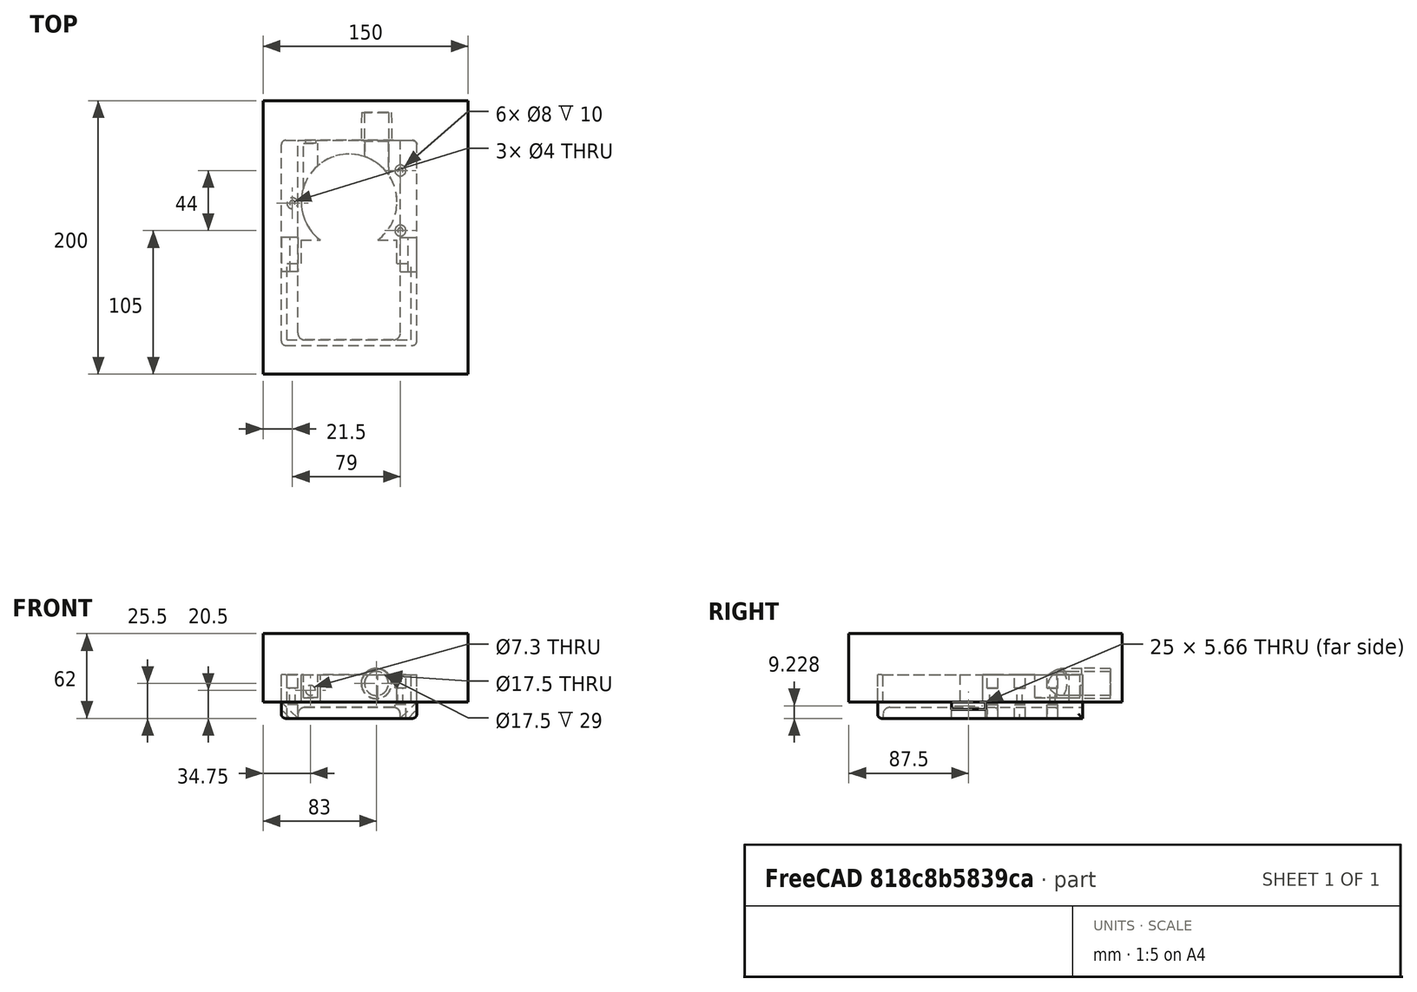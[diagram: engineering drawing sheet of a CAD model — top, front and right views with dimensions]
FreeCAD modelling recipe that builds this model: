
FCSTD DOCUMENT  (FreeCAD 0.18R4 (GitTag))
Label: PAPR-LOWER-V2
License: All rights reserved
LicenseURL: http://en.wikipedia.org/wiki/All_rights_reserved
objects: Part::Cylinder×17, Part::MultiFuse×11, Part::Box×8, Part::Fillet×7, Part::Cut×3, Part::Cone×2, Part::FeaturePython×1, Part::Mirroring×1
note: 50 computed .brp shape members not serialized (recipe doc carries the construction recipe); baked Part::Feature solids carry a one-line shape summary decoded from their .brp

FEATURE [Part::Cylinder] Cylinder  label="BlowerBody"
  Angle = 360
  AttacherType = Attacher::AttachEngine3D
  Height = 18
  Placement = pos=(0,0,4.5) rot=(0,0,1;0rad)
  Radius = 35
FEATURE [Part::Cylinder] Cylinder001  label="BlowerEndbearing"
  Angle = 360
  AttacherType = Attacher::AttachEngine3D
  Height = 5
  Placement = pos=(0,0,1) rot=(0,0,1;0rad)
  Radius = 2.25
FEATURE [Part::Cylinder] Cylinder002
  Angle = 360
  AttacherType = Attacher::AttachEngine3D
  Height = 10
  Placement = pos=(0,-28.4,0) rot=(0,0,1;0rad)
  Radius = 2
FEATURE [Part::FeaturePython] Array  label="BlowerFeet"  # Draft array (typed FeaturePython)
  Angle = 360
  ArrayType = 1
  Axis = (0,0,1)
  Base = -> Cylinder002
  Center = (0,0,0)
  Fuse = false
  IntervalAxis = (0,0,0)
  IntervalX = (1,0,0)
  IntervalY = (0,1,0)
  IntervalZ = (0,0,1)
  NumberPolar = 3
  NumberX = 1
  NumberY = 1
  NumberZ = 1
FEATURE [Part::Cylinder] Cylinder003  label="BlowerOutlet"
  Angle = 360
  AttacherType = Attacher::AttachEngine3D
  Height = 40
  Placement = pos=(20,36.3,13.5) rot=(1,0,0;1.5708rad)
  Radius = 8.75
FEATURE [Part::Cone] Cone  label="BlowerInlet"
  Angle = 360
  AttacherType = Attacher::AttachEngine3D
  Height = 13
  Placement = pos=(0,0,22.5) rot=(0,0,1;0rad)
  Radius1 = 27.25
  Radius2 = 27.15
FEATURE [Part::Cylinder] Cylinder004  label="BlowerBodyEnvelope"
  Angle = 360
  AttacherType = Attacher::AttachEngine3D
  Height = 25
  Radius = 35
FEATURE [Part::Cylinder] Cylinder005  label="OutletExtension"
  Angle = 360
  AttacherType = Attacher::AttachEngine3D
  Height = 40
  Placement = pos=(20,65.3,13.5) rot=(1,0,0;1.5708rad)
  Radius = 8.75
FEATURE [Part::Box] Box  label="DriverPocket"
  AttacherType = Attacher::AttachEngine3D
  Height = 20
  Length = 91
  Placement = pos=(-45.5,-106,0) rot=(0,0,1;0rad)
  Width = 56
FEATURE [Part::Box] Box001  label="WiringPocket"
  AttacherType = Attacher::AttachEngine3D
  Height = 20
  Length = 70
  Placement = pos=(-35,-53,0) rot=(0,0,1;0rad)
  Width = 20
FEATURE [Part::MultiFuse] Fusion  label="ElectronicsPocket"
  Placement = pos=(0,5,0) rot=(0,0,1;0rad)
  Shapes = -> [Box,Box001]
FEATURE [Part::Box] Box002  label="Potentiometer"
  AttacherType = Attacher::AttachEngine3D
  Height = 17
  Length = 10.5
  Placement = pos=(-30,18,5.5) rot=(0,0,1;0rad)
  Width = 35
FEATURE [Part::Cylinder] Cylinder006  label="Cylinder"
  Angle = 360
  AttacherType = Attacher::AttachEngine3D
  Height = 10
  Placement = pos=(-24.75,60.5,11) rot=(1,0,0;1.5708rad)
  Radius = 3.65
FEATURE [Part::MultiFuse] Fusion001  label="PotPocket"
  Placement = pos=(-3.5,-10,-2.5) rot=(0,0,1;0rad)
  Shapes = -> [Cylinder006,Box002]
FEATURE [Part::Box] Box003  label="Cube"
  AttacherType = Attacher::AttachEngine3D
  Height = 25
  Length = 75
  Placement = pos=(-37.5,-101,-29) rot=(0,0,1;0rad)
  Width = 150
FEATURE [Part::Fillet] Fillet
  Base = -> Box003
  Edges = 1 edges r=5: [Edge2]
FEATURE [Part::Fillet] Fillet001
  Base = -> Fillet
  Edges = 1 edges r=5: [Edge3]
FEATURE [Part::Fillet] Fillet002
  Base = -> Fillet001
  Edges = 1 edges r=5: [Edge17]
FEATURE [Part::Fillet] Fillet003
  Base = -> Fillet002
  Edges = 1 edges r=5: [Edge15]
FEATURE [Part::Fillet] Fillet004
  Base = -> Fillet003
  Edges = 1 edges r=5: [Edge18]
FEATURE [Part::Fillet] Fillet005  label="BatteryPocket"
  Base = -> Fillet004
  Edges = 4 edges r=5: [Edge3,Edge12,Edge13,Edge16]
FEATURE [Part::Box] Box004  label="HousingBlock"
  AttacherType = Attacher::AttachEngine3D
  Height = 32
  Length = 99
  Placement = pos=(-49.5,-105,-12) rot=(0,0,1;0rad)
  Width = 150
FEATURE [Part::Cylinder] Cylinder007  label="HousingOutlet"
  Angle = 360
  AttacherType = Attacher::AttachEngine3D
  Height = 40
  Placement = pos=(20,59.3,13.5) rot=(1,0,0;1.5708rad)
  Radius = 10.75
FEATURE [Part::MultiFuse] Fusion003  label="BlowerPocket"
  Shapes = -> [Cylinder004,Cone,Cylinder003,Array,Cylinder001,Cylinder]
FEATURE [Part::MultiFuse] Fusion004  label="CombinedPocket"
  Shapes = -> [Cylinder005,Fusion,Fusion001,Fillet005,Fusion003]
FEATURE [Part::Cone] Cone001  label="22mmTaper"
  Angle = 360
  AttacherType = Attacher::AttachEngine3D
  Height = 21
  Placement = pos=(20,65.3,13.5) rot=(0,-0.707107,0.707107;3.14159rad)
  Radius1 = 10.92
  Radius2 = 11.19
FEATURE [Part::MultiFuse] Fusion005  label="HousingLowerBody"
  Shapes = -> [Cone001,Cylinder007,Box004]
FEATURE [Part::Cut] Cut
  Base = -> Fusion005
  Tool = -> Fusion004
FEATURE [Part::Cylinder] Cylinder008  label="Cylinder003"
  Angle = 360
  AttacherType = Attacher::AttachEngine3D
  Height = 10
  Placement = pos=(-41.5,-1,10) rot=(0,0,1;0rad)
  Radius = 4
FEATURE [Part::Cylinder] Cylinder009  label="Cylinder004"
  Angle = 360
  AttacherType = Attacher::AttachEngine3D
  Height = 10
  Placement = pos=(37.5,-21,10) rot=(0,0,1;0rad)
  Radius = 4
FEATURE [Part::Cylinder] Cylinder010  label="Cylinder005"
  Angle = 360
  AttacherType = Attacher::AttachEngine3D
  Height = 10
  Placement = pos=(37.5,23,10) rot=(0,0,1;0rad)
  Radius = 4
FEATURE [Part::MultiFuse] Fusion006  label="TopMounting"
  Shapes = -> [Cylinder008,Cylinder009,Cylinder010]
FEATURE [Part::Cylinder] Cylinder011  label="Cylinder006"
  Angle = 360
  AttacherType = Attacher::AttachEngine3D
  Height = 30
  Placement = pos=(37.5,-21,10) rot=(0,0,1;0rad)
  Radius = 2
FEATURE [Part::Cylinder] Cylinder012  label="Cylinder007"
  Angle = 360
  AttacherType = Attacher::AttachEngine3D
  Height = 30
  Placement = pos=(37.5,23,10) rot=(0,0,1;0rad)
  Radius = 2
FEATURE [Part::Cylinder] Cylinder013  label="Cylinder008"
  Angle = 360
  AttacherType = Attacher::AttachEngine3D
  Height = 30
  Placement = pos=(-41.5,-1,10) rot=(0,0,1;0rad)
  Radius = 2
FEATURE [Part::MultiFuse] Fusion007  label="Mounting001"
  Placement = pos=(0,0,-30) rot=(0,0,1;0rad)
  Shapes = -> [Cylinder013,Cylinder011,Cylinder012]
FEATURE [Part::Cylinder] Cylinder014  label="Cylinder009"
  Angle = 360
  AttacherType = Attacher::AttachEngine3D
  Height = 20
  Placement = pos=(37.5,-21,10) rot=(0,0,1;0rad)
  Radius = 4
FEATURE [Part::Cylinder] Cylinder015  label="Cylinder010"
  Angle = 360
  AttacherType = Attacher::AttachEngine3D
  Height = 20
  Placement = pos=(37.5,23,10) rot=(0,0,1;0rad)
  Radius = 4
FEATURE [Part::Cylinder] Cylinder016  label="Cylinder011"
  Angle = 360
  AttacherType = Attacher::AttachEngine3D
  Height = 20
  Placement = pos=(-41.5,-1,10) rot=(0,0,1;0rad)
  Radius = 4
FEATURE [Part::MultiFuse] Fusion008  label="Mounting002"
  Placement = pos=(0,0,-32) rot=(0,0,1;0rad)
  Shapes = -> [Cylinder016,Cylinder014,Cylinder015]
FEATURE [Part::MultiFuse] Fusion009  label="BottomMounting"
  Shapes = -> [Fusion007,Fusion008]
FEATURE [Part::MultiFuse] Fusion010  label="CombinedMounting"
  Shapes = -> [Fusion006,Fusion009]
FEATURE [Part::Cut] Cut001
  Base = -> Cut
  Tool = -> Fusion010
FEATURE [Part::Box] Box005  label="Slot1"
  AttacherType = Attacher::AttachEngine3D
  Height = 4
  Length = 25
  Placement = pos=(-37.4228,-51,-17.6777) rot=(0.357407,0.357407,0.862856;1.71777rad)
  Width = 40
FEATURE [Part::Box] Box006  label="Slot2"
  AttacherType = Attacher::AttachEngine3D
  Height = 4
  Length = 25
  Placement = pos=(-37.4228,-44,-17.6777) rot=(0.357407,0.357407,0.862856;1.71777rad)
  Width = 40
FEATURE [Part::Mirroring] Part__Mirroring  label="Slot2 (Mirror #1)"
  Base = (0,0,0)
  Normal = (1,0,0)
  Placement = pos=(0,-7,0) rot=(0,0,1;0rad)
  Source = -> Box006
FEATURE [Part::MultiFuse] Fusion011  label="StrapSlots"
  Shapes = -> [Box005,Part__Mirroring]
FEATURE [Part::Cut] Cut002  label="PAPR-Lower-Housing"
  Base = -> Cut001
  Tool = -> Fusion011
FEATURE [Part::Box] Box007  label="Cube001"
  AttacherType = Attacher::AttachEngine3D
  Height = 50
  Length = 150
  Placement = pos=(-63,-126,0) rot=(0,0,1;0rad)
  Width = 200
FEATURE [Part::Fillet] Fillet006
  Base = -> Cut002
  Edges = 7 edges r=3: [Edge37,Edge45,Edge51,Edge52,Edge57,Edge58,Edge59]
